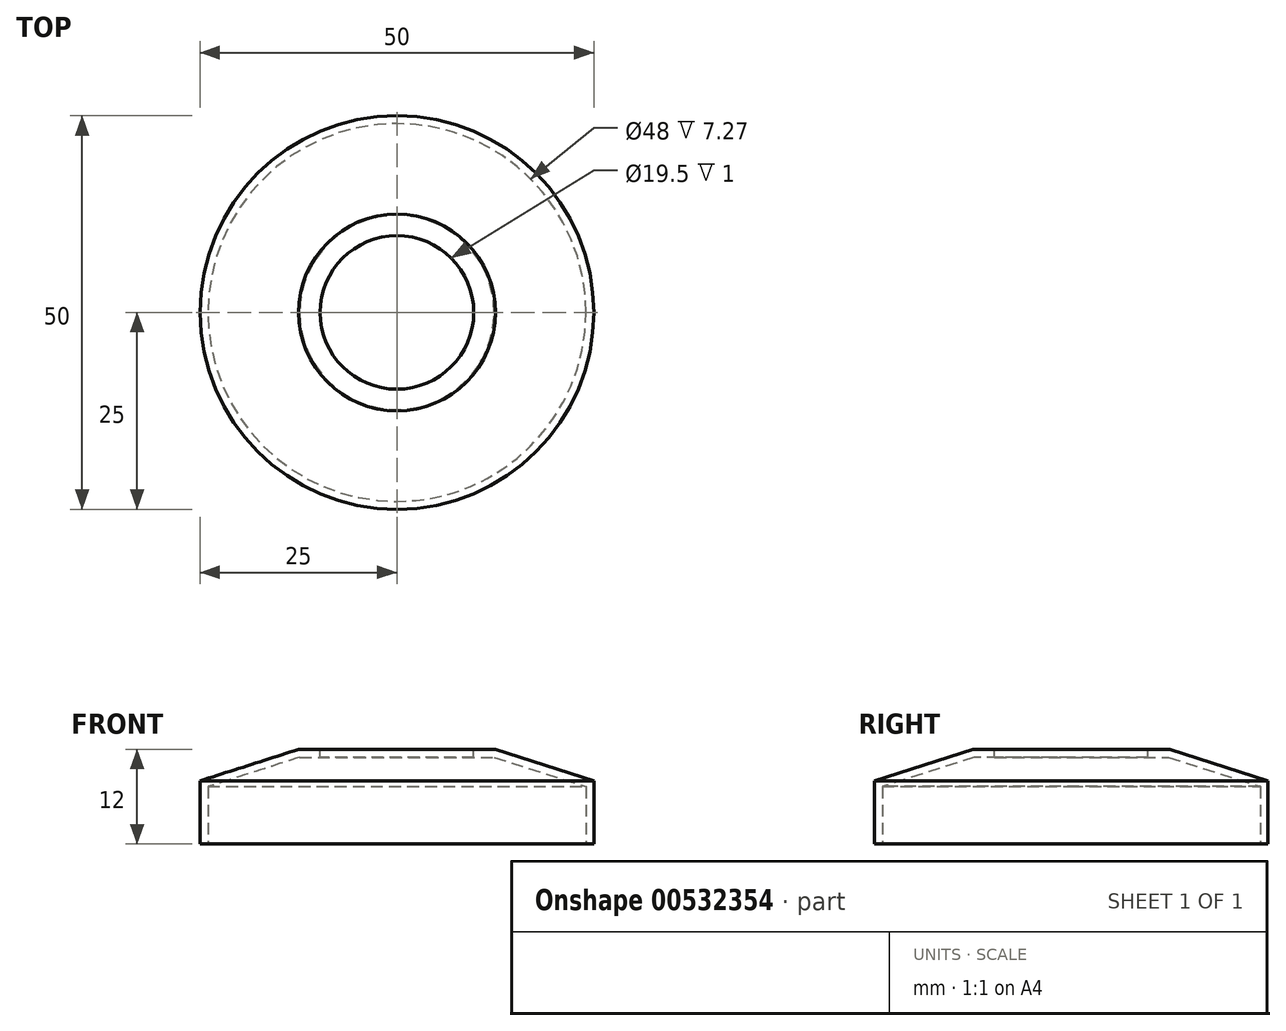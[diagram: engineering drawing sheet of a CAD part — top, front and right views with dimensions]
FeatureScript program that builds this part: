
annotation { "Feature Type Name" : "Feature", "Feature Type Description" : "" }
export const myFeature = defineFeature(function(context is Context, id is Id, definition is map)
    precondition{}
    {
        {
            var Q0;
            Q0=qCreatedBy(makeId("Front.planeOp"),FACE);
            var sketch = newSketch(context, id + "F0", { "sketchPlane" : qUnion([Q0])});
            skLineSegment(sketch, "E0", {"start": v(0, 0) * mm, "end": v(0, 78.35) * mm, "construction": true});
            skLineSegment(sketch, "E1", {"start": v(0, 0) * mm, "end": v(25, 0) * mm});
            skLineSegment(sketch, "E2", {"start": v(25, 0) * mm, "end": v(25, 8) * mm});
            skLineSegment(sketch, "E3", {"start": v(25, 8) * mm, "end": v(12.5, 12) * mm});
            skLineSegment(sketch, "E4", {"start": v(12.5, 12) * mm, "end": v(0, 12) * mm});
            skLineSegment(sketch, "E5", {"start": v(0, 12) * mm, "end": v(0, 0) * mm});
            skSolve(sketch);
        }
        {
            var Q0;
            Q0=makeQuery(id+"F0.imprint","IMPRINT",FACE,{"disambiguationData":[TD([[makeQuery(id+"F0.imprint","IMPRINT",EDGE,{"derivedFrom":sQuery(id+"F0.wireOp",EDGE,"E1")}),1.0]])]});
            var Q1;
            Q1=sQuery(id+"F0.wireOp",EDGE,"E0");
            revolve(context, id + "F1", {"entities" : qUnion([Q0]), "axis" : qUnion([Q1]), "revolveType" : RevolveType.FULL});
        }
        {
            var Q0;
            Q0=makeQuery(id+"F1.opRevolve","SWEPT_FACE",FACE,{"disambiguationData":[OSD([sQuery(id+"F0.wireOp",EDGE,"E1")])]});
            shell(context, id + "F2", {"entities" : qUnion([Q0]), "thickness" : 1 * mm});
        }
        {
            var Q0;
            Q0=makeQuery(id+"F1.opRevolve","SWEPT_FACE",FACE,{"disambiguationData":[OSD([sQuery(id+"F0.wireOp",EDGE,"E4")])]});
            var sketch = newSketch(context, id + "F3", { "sketchPlane" : qUnion([Q0])});
            skCircle(sketch, "E6", {"center": v(0, 0) * mm, "radius": 9.75 * mm});
            skSolve(sketch);
        }
        {
            var Q0;
            Q0=qSketchRegion(id+"F3",true);
            extrude(context, id + "F4", {"entities" : qUnion([Q0]), "operationType" : NewBodyOperationType.REMOVE, "endBound" : BoundingType.UP_TO_NEXT, "oppositeDirection" : true, "depth" : 25 * mm});
        }
    });
